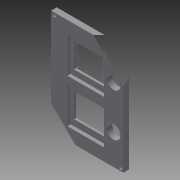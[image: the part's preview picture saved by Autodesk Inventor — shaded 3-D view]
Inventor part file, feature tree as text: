
AUTODESK INVENTOR PART (.ipt)
format: ipt  version: 2015 (Build 190159000, 159)  size: 200,704 bytes
history: native  units: in
note: dims shown in document units (in); Inventor stores cm internally (conversion verified against a paired STEP export)
features: reference x37, extrude x5, sketch x5
ambient origin geometry x8: Origin, YZ Plane, XZ Plane, XY Plane, X Axis, Y Axis, Z Axis, Center Point
bodies: Solid1 (feature_tree)
feature tree (47):
  extrude  "Extrusion1"  Depth=0.4356in
  extrude  "Extrusion2"  Depth=0.5723in
  extrude  "Extrusion3"  Depth=0.6876in
  extrude  "Extrusion4"  Depth=1.2795in
  extrude  "Extrusion5"  Depth=0.1181in TaperAngle=0.0deg
  sketch  "Sketch1"  dims[d0=0.1969in d1=0.0in d2=0.4356in]
  reference  "Reference1"
  reference  "Reference2"
  reference  "Reference3"
  reference  "Reference4"
  reference  "Reference5"
  reference  "Reference6"
  reference  "Reference7"
  reference  "Reference8"
  reference  "Reference9"
  reference  "Reference10"
  reference  "Reference11"
  reference  "Reference12"
  sketch  "Sketch2"  dims[d3=0.6876in d4=0.5723in]
  sketch  "Sketch3"  dims[d5=0.4356in d6=0.6876in]
  reference  "Reference17"
  reference  "Reference18"
  reference  "Reference19"
  reference  "Reference20"
  reference  "Reference21"
  reference  "Reference22"
  reference  "Reference23"
  reference  "Reference24"
  reference  "Reference25"
  reference  "Reference26"
  reference  "Reference27"
  reference  "Reference28"
  reference  "Reference29"
  reference  "Reference30"
  reference  "Reference31"
  reference  "Reference32"
  reference  "Reference33"
  sketch  "Sketch4"  dims[d7=0.5723in d8=1.2795in]
  reference  "Reference35"
  reference  "Reference36"
  sketch  "Sketch5"  dims[d9=1.2795in d10=0.1181in d11=0.0in d12=0.0787in d13=0.0787in d14=0.0787in d15=0.0787in d16=0.1181in d17=0.0in d18=0.2421in d19=0.344in d20=0.1181in d21=0.0in d24=0.1181in d25=0.0in]
  reference  "Reference39"
  reference  "Reference40"
  reference  "Reference41"
  reference  "Reference42"
  reference  "Reference44"
  reference  "Reference46"
